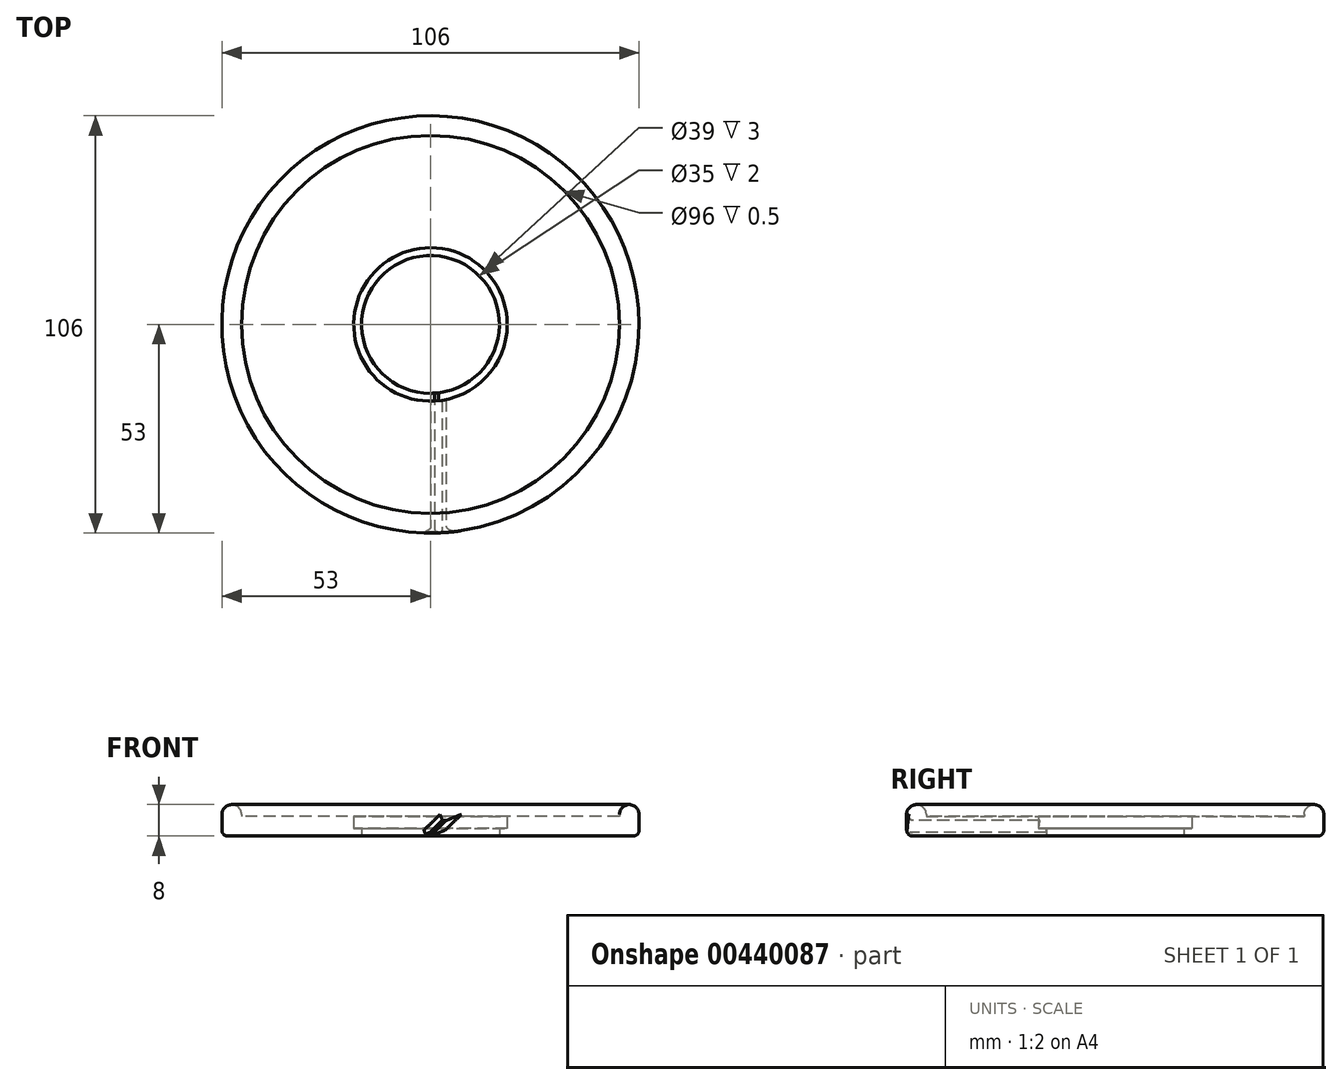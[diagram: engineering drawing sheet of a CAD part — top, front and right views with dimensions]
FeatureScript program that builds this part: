
annotation { "Feature Type Name" : "Feature", "Feature Type Description" : "" }
export const myFeature = defineFeature(function(context is Context, id is Id, definition is map)
    precondition{}
    {
        {
            var Q0;
            Q0=qCreatedBy(makeId("Top.planeOp"),FACE);
            var sketch = newSketch(context, id + "F0", { "sketchPlane" : qUnion([Q0])});
            skCircle(sketch, "E0", {"center": v(0, 0) * mm, "radius": 48 * mm});
            skCircle(sketch, "E1", {"center": v(0, 0) * mm, "radius": 53 * mm});
            skCircle(sketch, "E2", {"center": v(0, 0) * mm, "radius": 19.5 * mm});
            skCircle(sketch, "E3", {"center": v(0, 0) * mm, "radius": 17.5 * mm});
            skSolve(sketch);
        }
        {
            var Q0;
            Q0 = qSketchRegion(id + "F0", true);
            extrude(context, id + "F1", {"entities" : qUnion([Q0]), "depth" : 8 * mm});
        }
        {
            var Q0;
            Q0=makeQuery(id+"F0.imprint","IMPRINT",FACE,{"disambiguationData":[TD([[makeQuery(id+"F0.imprint","IMPRINT",EDGE,{"derivedFrom":sQuery(id+"F0.wireOp",EDGE,"E0")}),1.0]])]});
            extrude(context, id + "F2", {"entities" : qUnion([Q0]), "operationType" : NewBodyOperationType.ADD, "depth" : 5 * mm});
        }
        {
            var Q0;
            Q0=makeQuery(id+"F0.imprint","IMPRINT",FACE,{"disambiguationData":[TD([[makeQuery(id+"F0.imprint","IMPRINT",EDGE,{"derivedFrom":sQuery(id+"F0.wireOp",EDGE,"E2")}),1.0]])]});
            extrude(context, id + "F3", {"entities" : qUnion([Q0]), "operationType" : NewBodyOperationType.ADD, "depth" : 2 * mm});
        }
        {
            var Q0;
            Q0=qCreatedBy(makeId("Front.planeOp"),FACE);
            cPlane(context, id + "F4", {"entities" : qUnion([Q0]), "cplaneType" : CPlaneType.OFFSET, "offset" : 53 * mm, "width" : 150 * mm, "height" : 150 * mm});
        }
        {
            var Q0;
            Q0=qCreatedBy(id+"F4.planeOp",FACE);
            var sketch = newSketch(context, id + "F5", { "sketchPlane" : qUnion([Q0])});
            skLineSegment(sketch, "E4", {"start": v(0, 1) * mm, "end": v(3, 4) * mm});
            skLineSegment(sketch, "E5", {"start": v(3, 4) * mm, "end": v(4, 4) * mm});
            skLineSegment(sketch, "E6", {"start": v(4, 4) * mm, "end": v(1, 1) * mm});
            skLineSegment(sketch, "E7", {"start": v(1, 1) * mm, "end": v(0, 1) * mm});
            skSolve(sketch);
        }
        {
            var Q0;
            Q0 = qSketchRegion(id + "F5", true);
            extrude(context, id + "F6", {"entities" : qUnion([Q0]), "operationType" : NewBodyOperationType.REMOVE, "oppositeDirection" : true, "depth" : 49.8 * mm});
        }
        {
            var Q0;
            Q0=makeQuery(id+"F1.opExtrude","CAP_EDGE",EDGE,{"disambiguationData":[OSD([sQuery(id+"F0.wireOp",EDGE,"E1")])],"isStart":false});
            var Q1;
            Q1=makeQuery(id+"F1.opExtrude","CAP_EDGE",EDGE,{"disambiguationData":[OSD([sQuery(id+"F0.wireOp",EDGE,"E0")])],"isStart":false});
            fillet(context, id + "F7", {"entities" : qUnion([Q0, Q1]), "radius" : 2.5 * mm, "tangentPropagation" : true, "allowEdgeOverflow" : false});
        }
        {
            var Q0;
            Q0=makeQuery(id+"FyVVZFpzCP2ymNz_1.13.F6.boolean.opBoolean","INTERSECT",EDGE,{"derivedFrom":[makeQuery(id+"F1.opExtrude","SWEPT_FACE",FACE,{"disambiguationData":[OSD([sQuery(id+"F0.wireOp",EDGE,"E1")])]}),makeQuery(id+"FyVVZFpzCP2ymNz_1.13.F6.opExtrude","SWEPT_FACE",FACE,{"disambiguationData":[OSD([sQuery(id+"F5.wireOp",EDGE,"E6")])]})]});
            var Q1;
            Q1=makeQuery(id+"F1.opExtrude","SWEPT_FACE",FACE,{"disambiguationData":[OSD([sQuery(id+"F0.wireOp",EDGE,"E1")])]});
            fillet(context, id + "F8", {"entities" : qUnion([Q0, Q1]), "radius" : 1.5 * mm, "tangentPropagation" : true, "allowEdgeOverflow" : false});
        }
    });
